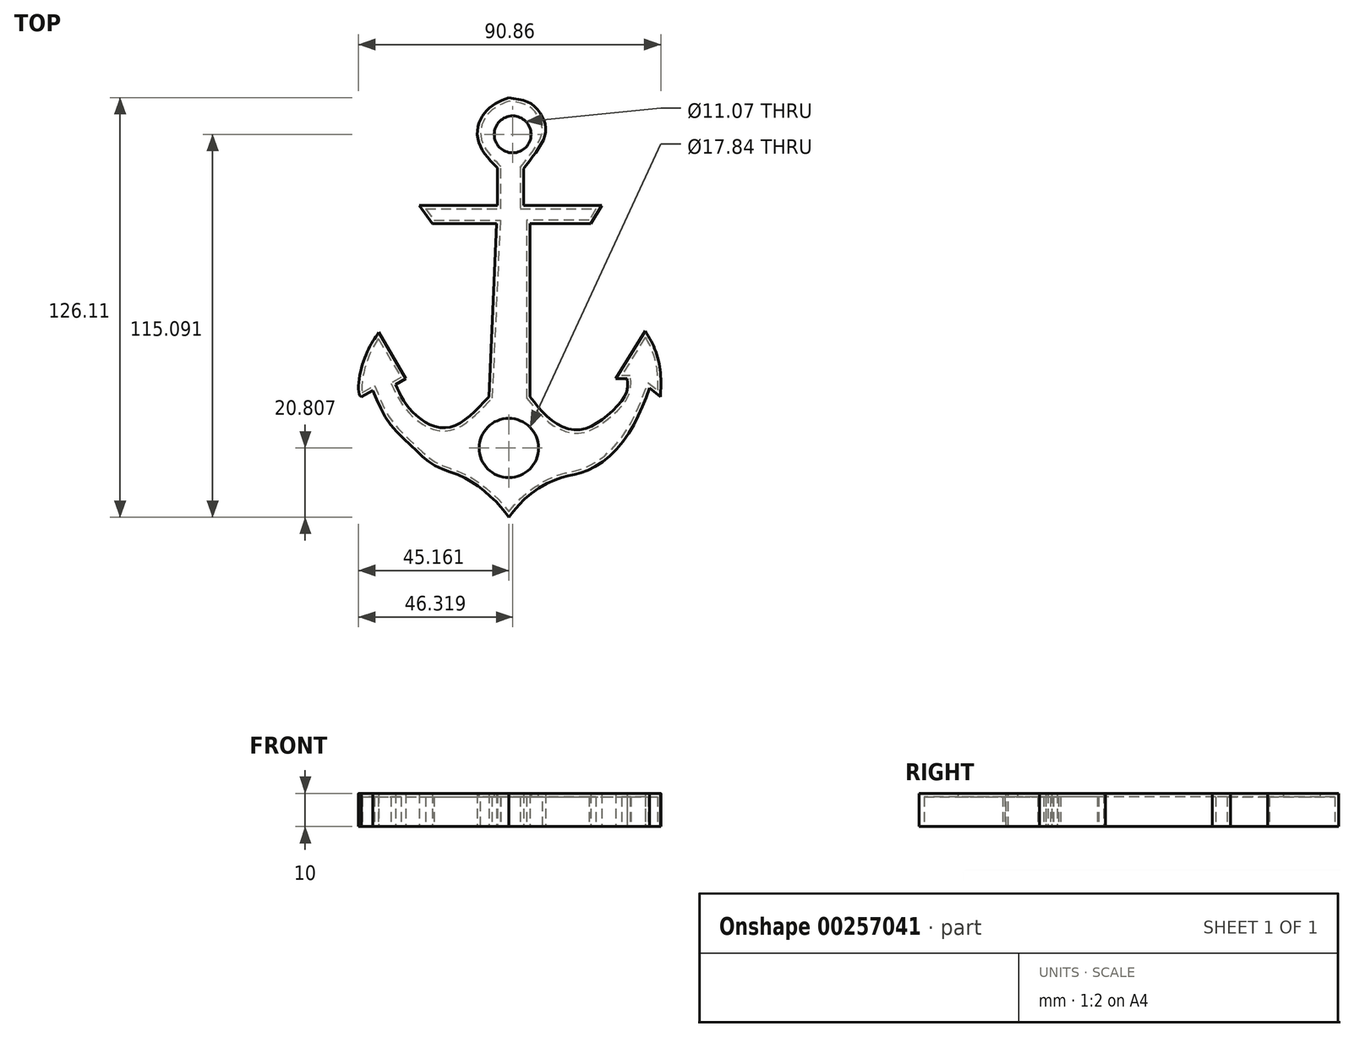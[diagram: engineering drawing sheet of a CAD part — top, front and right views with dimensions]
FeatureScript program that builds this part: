
annotation { "Feature Type Name" : "Feature", "Feature Type Description" : "" }
export const myFeature = defineFeature(function(context is Context, id is Id, definition is map)
    precondition{}
    {
        {
            var Q0;
            Q0=qCreatedBy(makeId("Top.planeOp"),FACE);
            var sketch = newSketch(context, id + "F0", { "sketchPlane" : qUnion([Q0])});
            skLineSegment(sketch, "E0", {"start": v(-11.68, 33.64) * mm, "end": v(11.83, 33.64) * mm});
            skLineSegment(sketch, "E1", {"start": v(-11.68, 33.64) * mm, "end": v(-7.76, 28.2) * mm});
            skLineSegment(sketch, "E2", {"start": v(-7.76, 28.2) * mm, "end": v(11.62, 28.2) * mm});
            skLineSegment(sketch, "E3", {"start": v(11.62, 28.2) * mm, "end": v(9.22, -23.84) * mm});
            skLineSegment(sketch, "E4", {"start": v(11.83, 33.64) * mm, "end": v(11.83, 44.96) * mm});
            skLineSegment(sketch, "E5", {"start": v(19.67, 44.74) * mm, "end": v(19.67, 33.64) * mm});
            skLineSegment(sketch, "E6", {"start": v(19.67, 33.64) * mm, "end": v(43.19, 33.64) * mm});
            skLineSegment(sketch, "E7", {"start": v(43.19, 33.64) * mm, "end": v(39.92, 28.2) * mm});
            skLineSegment(sketch, "E8", {"start": v(39.92, 28.2) * mm, "end": v(21.63, 28.2) * mm});
            skLineSegment(sketch, "E9", {"start": v(21.63, 28.2) * mm, "end": v(21.63, -23.84) * mm});
            skLineSegment(sketch, "E10", {"start": v(47.32, -18.4) * mm, "end": v(50.8, -18.4) * mm});
            skLineSegment(sketch, "E11", {"start": v(57.55, -21.23) * mm, "end": v(60.82, -23.84) * mm});
            skLineSegment(sketch, "E12", {"start": v(-15.82, -18.4) * mm, "end": v(-18.86, -20.14) * mm});
            skLineSegment(sketch, "E13", {"start": v(-29.1, -23.84) * mm, "end": v(-25.61, -21.88) * mm});
            skLineSegment(sketch, "E14", {"start": v(-23.87, -4.46) * mm, "end": v(-15.82, -18.4) * mm});
            skLineSegment(sketch, "E15", {"start": v(56.25, -4.03) * mm, "end": v(47.32, -18.4) * mm});
            skLineSegment(sketch, "E16", {"start": v(-50, -23.84) * mm, "end": v(-50, -21.88) * mm});
            skFitSpline(sketch, "E17", {"points": [v(-23.87, -4.46) * mm, v(-27.03, -9.64) * mm, v(-29.8, -18.93) * mm, v(-29.1, -23.84) * mm, v(-25.61, -21.88) * mm], "startDerivative": vector(-12.9, -18.55) * mm, "endDerivative": vector(19.98, 16.88) * mm});
            skFitSpline(sketch, "E18", {"points": [v(56.25, -4.03) * mm, v(59.25, -9.8) * mm, v(60.82, -16.98) * mm, v(60.82, -23.84) * mm], "startDerivative": vector(10.2, -17.04) * mm, "endDerivative": vector(-0.88, -20.38) * mm});
            skFitSpline(sketch, "E19", {"points": [v(-18.86, -20.14) * mm, v(-13.98, -28.07) * mm, v(-3.54, -33.12) * mm, v(9.22, -23.84) * mm], "startDerivative": vector(12.93, -27.71) * mm, "endDerivative": vector(32.8, 34.92) * mm});
            skFitSpline(sketch, "E20", {"points": [v(21.63, -23.84) * mm, v(28.26, -31) * mm, v(36.25, -33.78) * mm, v(44.24, -29.86) * mm, v(50.44, -22.84) * mm, v(50.8, -18.4) * mm], "startDerivative": vector(27.6, -35.73) * mm, "endDerivative": vector(-2.89, 28.87) * mm});
            skFitSpline(sketch, "E21", {"points": [v(-25.61, -21.88) * mm, v(-20.5, -31.98) * mm, v(-13.17, -39.49) * mm, v(-7.3, -44.38) * mm, v(0, -47.31) * mm, v(6.24, -50.9) * mm, v(11.95, -55.96) * mm, v(15.21, -60.04) * mm], "startDerivative": vector(25.67, -62.97) * mm, "endDerivative": vector(25.5, -34.8) * mm});
            skFitSpline(sketch, "E22", {"points": [v(15.21, -60.04) * mm, v(21.25, -53.51) * mm, v(30.38, -48.3) * mm, v(35.93, -46.99) * mm, v(43.76, -43.07) * mm, v(52.07, -33.45) * mm, v(57.55, -21.23) * mm], "startDerivative": vector(33.33, 42.22) * mm, "endDerivative": vector(24.55, 64.43) * mm});
            skFitSpline(sketch, "E23", {"points": [v(19.67, 44.74) * mm, v(22.73, 48.77) * mm, v(26.19, 55) * mm, v(25.5, 59.84) * mm, v(22.03, 64.23) * mm, v(15.21, 66.07) * mm], "startDerivative": vector(15.47, 20.04) * mm, "endDerivative": vector(-34.25, 4.7) * mm});
            skFitSpline(sketch, "E24", {"points": [v(15.21, 66.07) * mm, v(10.04, 63.53) * mm, v(6.35, 58.7) * mm, v(6.35, 52.23) * mm, v(11.83, 44.96) * mm], "startDerivative": vector(-23.51, -8.97) * mm, "endDerivative": vector(23.35, -24.45) * mm});
            skSolve(sketch);
        }
        {
            var Q0;
            Q0=makeQuery(id+"F0.imprint","IMPRINT",FACE,{"disambiguationData":[TD([[makeQuery(id+"F0.imprint","IMPRINT",EDGE,{"derivedFrom":sQuery(id+"F0.wireOp",EDGE,"E0")}),-1.0]])]});
            extrude(context, id + "F1", {"entities" : qUnion([Q0]), "depth" : 10 * mm});
        }
        {
            var Q0;
            Q0=makeQuery(id+"F1.opExtrude","CAP_FACE",FACE,{"disambiguationData":[OSD([sQuery(id+"F0.wireOp",EDGE,"E0"),sQuery(id+"F0.wireOp",EDGE,"E1"),sQuery(id+"F0.wireOp",EDGE,"E2"),sQuery(id+"F0.wireOp",EDGE,"E3"),sQuery(id+"F0.wireOp",EDGE,"E4"),sQuery(id+"F0.wireOp",EDGE,"E5"),sQuery(id+"F0.wireOp",EDGE,"E6"),sQuery(id+"F0.wireOp",EDGE,"E7"),sQuery(id+"F0.wireOp",EDGE,"E8"),sQuery(id+"F0.wireOp",EDGE,"E9"),sQuery(id+"F0.wireOp",EDGE,"E10"),sQuery(id+"F0.wireOp",EDGE,"E11"),sQuery(id+"F0.wireOp",EDGE,"E12"),sQuery(id+"F0.wireOp",EDGE,"E13"),sQuery(id+"F0.wireOp",EDGE,"E14"),sQuery(id+"F0.wireOp",EDGE,"E15"),sQuery(id+"F0.wireOp",EDGE,"E17"),sQuery(id+"F0.wireOp",EDGE,"E18"),sQuery(id+"F0.wireOp",EDGE,"E19"),sQuery(id+"F0.wireOp",EDGE,"E20"),sQuery(id+"F0.wireOp",EDGE,"E21"),sQuery(id+"F0.wireOp",EDGE,"E22"),sQuery(id+"F0.wireOp",EDGE,"E23"),sQuery(id+"F0.wireOp",EDGE,"E24")])],"isStart":true});
            shell(context, id + "F2", {"entities" : qUnion([Q0]), "thickness" : 1 * mm});
        }
        {
            var Q0;
            Q0=makeQuery(id+"F2.opShell","OFFSET_FACE",FACE,{"disambiguationData":[OSD([sQuery(id+"F0.wireOp",EDGE,"E0"),sQuery(id+"F0.wireOp",EDGE,"E1"),sQuery(id+"F0.wireOp",EDGE,"E2"),sQuery(id+"F0.wireOp",EDGE,"E3"),sQuery(id+"F0.wireOp",EDGE,"E4"),sQuery(id+"F0.wireOp",EDGE,"E5"),sQuery(id+"F0.wireOp",EDGE,"E6"),sQuery(id+"F0.wireOp",EDGE,"E7"),sQuery(id+"F0.wireOp",EDGE,"E8"),sQuery(id+"F0.wireOp",EDGE,"E9"),sQuery(id+"F0.wireOp",EDGE,"E10"),sQuery(id+"F0.wireOp",EDGE,"E11"),sQuery(id+"F0.wireOp",EDGE,"E12"),sQuery(id+"F0.wireOp",EDGE,"E13"),sQuery(id+"F0.wireOp",EDGE,"E14"),sQuery(id+"F0.wireOp",EDGE,"E15"),sQuery(id+"F0.wireOp",EDGE,"E17"),sQuery(id+"F0.wireOp",EDGE,"E18"),sQuery(id+"F0.wireOp",EDGE,"E19"),sQuery(id+"F0.wireOp",EDGE,"E20"),sQuery(id+"F0.wireOp",EDGE,"E21"),sQuery(id+"F0.wireOp",EDGE,"E22"),sQuery(id+"F0.wireOp",EDGE,"E23"),sQuery(id+"F0.wireOp",EDGE,"E24")])]});
            var sketch = newSketch(context, id + "F3", { "sketchPlane" : qUnion([Q0])});
            skCircle(sketch, "E25", {"center": v(16.39, -55.05) * mm, "radius": 5.54 * mm});
            skPoint(sketch, "E25.first.point", {"position": v(19.65, -50.58) * mm});
            skPoint(sketch, "E25.second.point", {"position": v(11.34, -57.32) * mm});
            skPoint(sketch, "E25.third.point", {"position": v(19.33, -59.74) * mm});
            skSolve(sketch);
        }
        {
            var Q0;
            Q0 = qSketchRegion(id + "F3", true);
            extrude(context, id + "F4", {"entities" : qUnion([Q0]), "operationType" : NewBodyOperationType.REMOVE, "oppositeDirection" : true, "depth" : 25.4 * mm});
        }
        {
            var Q0;
            Q0=makeQuery(id+"F1.opExtrude","CAP_FACE",FACE,{"disambiguationData":[OSD([sQuery(id+"F0.wireOp",EDGE,"E0"),sQuery(id+"F0.wireOp",EDGE,"E1"),sQuery(id+"F0.wireOp",EDGE,"E2"),sQuery(id+"F0.wireOp",EDGE,"E3"),sQuery(id+"F0.wireOp",EDGE,"E4"),sQuery(id+"F0.wireOp",EDGE,"E5"),sQuery(id+"F0.wireOp",EDGE,"E6"),sQuery(id+"F0.wireOp",EDGE,"E7"),sQuery(id+"F0.wireOp",EDGE,"E8"),sQuery(id+"F0.wireOp",EDGE,"E9"),sQuery(id+"F0.wireOp",EDGE,"E10"),sQuery(id+"F0.wireOp",EDGE,"E11"),sQuery(id+"F0.wireOp",EDGE,"E12"),sQuery(id+"F0.wireOp",EDGE,"E13"),sQuery(id+"F0.wireOp",EDGE,"E14"),sQuery(id+"F0.wireOp",EDGE,"E15"),sQuery(id+"F0.wireOp",EDGE,"E17"),sQuery(id+"F0.wireOp",EDGE,"E18"),sQuery(id+"F0.wireOp",EDGE,"E19"),sQuery(id+"F0.wireOp",EDGE,"E20"),sQuery(id+"F0.wireOp",EDGE,"E21"),sQuery(id+"F0.wireOp",EDGE,"E22"),sQuery(id+"F0.wireOp",EDGE,"E23"),sQuery(id+"F0.wireOp",EDGE,"E24")])],"isStart":false});
            var sketch = newSketch(context, id + "F5", { "sketchPlane" : qUnion([Q0])});
            skCircle(sketch, "E26", {"center": v(15.23, -39.23) * mm, "radius": 8.92 * mm});
            skPoint(sketch, "E26.first.point", {"position": v(8.46, -33.42) * mm});
            skPoint(sketch, "E26.second.point", {"position": v(13.16, -47.9) * mm});
            skPoint(sketch, "E26.third.point", {"position": v(22.21, -33.68) * mm});
            skSolve(sketch);
        }
        {
            var Q0;
            Q0 = qSketchRegion(id + "F5", true);
            extrude(context, id + "F6", {"entities" : qUnion([Q0]), "operationType" : NewBodyOperationType.REMOVE, "oppositeDirection" : true, "depth" : 25.4 * mm});
        }
    });
